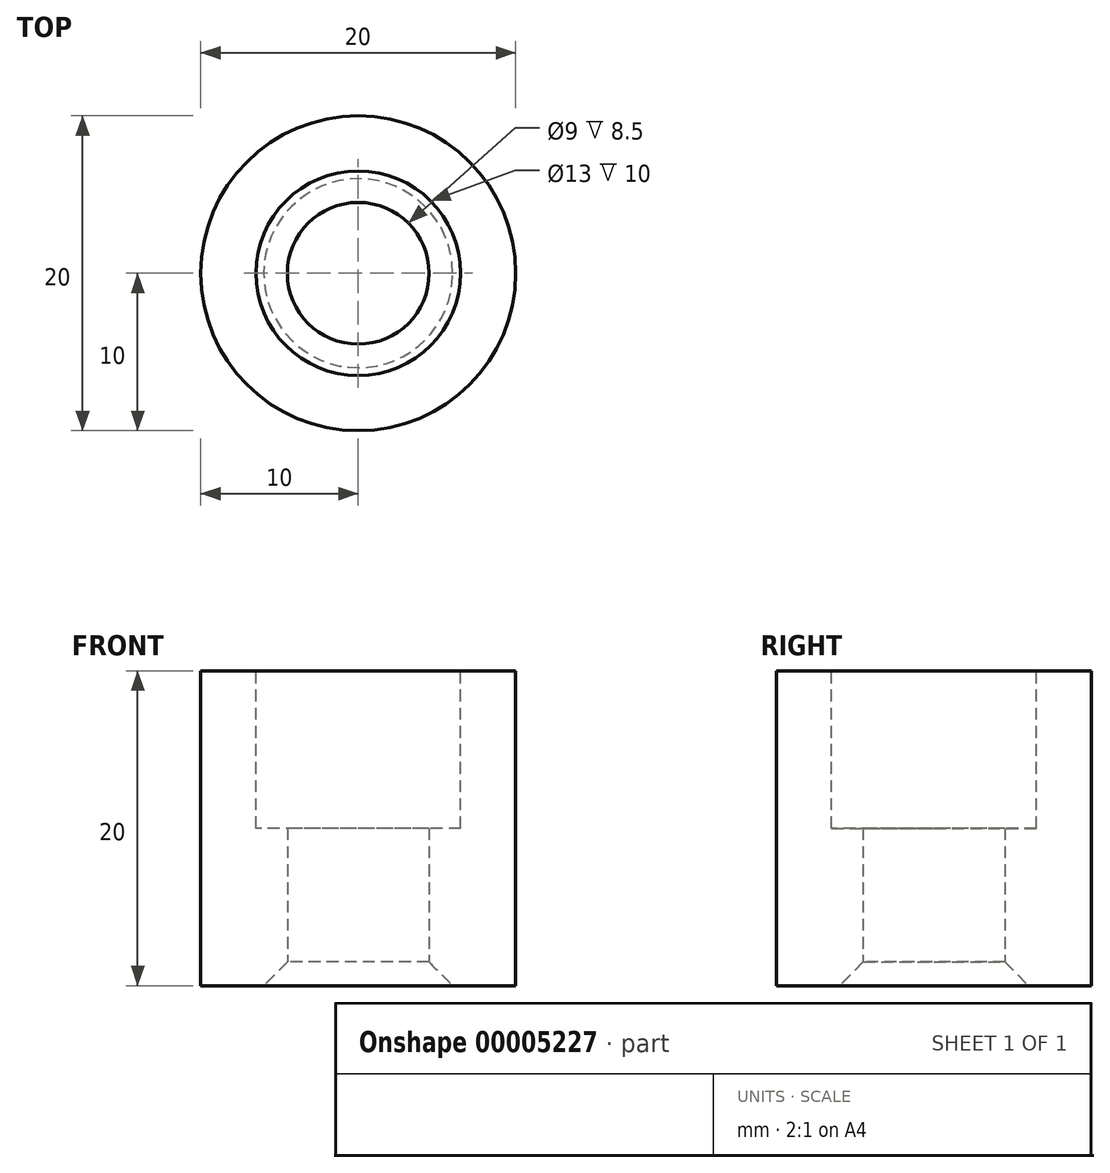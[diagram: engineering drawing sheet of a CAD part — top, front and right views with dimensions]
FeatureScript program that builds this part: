
annotation { "Feature Type Name" : "Feature", "Feature Type Description" : "" }
export const myFeature = defineFeature(function(context is Context, id is Id, definition is map)
    precondition{}
    {
        {
            var Q0;
            Q0=qCreatedBy(makeId("Top.planeOp"),FACE);
            var sketch = newSketch(context, id + "F0", { "sketchPlane" : qUnion([Q0])});
            skCircle(sketch, "E0", {"center": v(0, 0) * mm, "radius": 10 * mm});
            skCircle(sketch, "E1", {"center": v(0, 0) * mm, "radius": 4.5 * mm});
            skSolve(sketch);
        }
        {
            var Q0;
            Q0=makeQuery(id+"F0.imprint","IMPRINT",FACE,{"disambiguationData":[TD([[makeQuery(id+"F0.imprint","IMPRINT",EDGE,{"derivedFrom":sQuery(id+"F0.wireOp",EDGE,"E0")}),1.0]])]});
            extrude(context, id + "F1", {"entities" : qUnion([Q0]), "depth" : 10 * mm});
        }
        {
            var Q0;
            Q0=makeQuery(id+"F1.opExtrude","CAP_FACE",FACE,{"disambiguationData":[OSD([sQuery(id+"F0.wireOp",EDGE,"E0"),sQuery(id+"F0.wireOp",EDGE,"E1")])],"isStart":false});
            var sketch = newSketch(context, id + "F2", { "sketchPlane" : qUnion([Q0])});
            skCircle(sketch, "E2", {"center": v(0, 0) * mm, "radius": 6.5 * mm});
            skCircle(sketch, "E3", {"center": v(0, 0) * mm, "radius": 10 * mm});
            skSolve(sketch);
        }
        {
            var Q0;
            {var subQ0=makeQuery(id+"F2.imprint","IMPRINT",EDGE,{"derivedFrom":sQuery(id+"F2.wireOp",EDGE,"E2")});var subQ1=makeQuery(id+"F2.imprint","IMPRINT",EDGE,{"derivedFrom":makeQuery(id+"F1.opExtrude","CAP_EDGE",EDGE,{"disambiguationData":[OSD([sQuery(id+"F0.wireOp",EDGE,"E1")])],"isStart":false})});Q0=qUnion([makeQuery(id+"F2.imprint","IMPRINT",FACE,{"disambiguationData":[TD([[subQ0,-1.0]])]}),makeQuery(id+"F2.imprint","IMPRINT",FACE,{"disambiguationData":[TD([[subQ1,1.0]])]}),makeQuery(id+"F2.imprint","IMPRINT",FACE,{"disambiguationData":[TD([[subQ0,1.0]])]})]);}
            extrude(context, id + "F3", {"entities" : qUnion([Q0]), "operationType" : NewBodyOperationType.ADD, "depth" : 10 * mm});
        }
        {
            var Q0;
            Q0=makeQuery(id+"F3.opExtrude","CAP_FACE",FACE,{"disambiguationData":[OSD([sQuery(id+"F2.wireOp",EDGE,"E3")])],"isStart":false});
            var sketch = newSketch(context, id + "F4", { "sketchPlane" : qUnion([Q0])});
            skCircle(sketch, "E4", {"center": v(0, 0) * mm, "radius": 6.5 * mm});
            skSolve(sketch);
        }
        {
            var Q0;
            Q0=makeQuery(id+"F4.imprint","IMPRINT",FACE,{"disambiguationData":[TD([[makeQuery(id+"F4.imprint","IMPRINT",EDGE,{"derivedFrom":sQuery(id+"F4.wireOp",EDGE,"E4")}),1.0]])]});
            var Q1;
            Q1=makeQuery(id+"F3.opExtrude","CAP_FACE",FACE,{"disambiguationData":[OSD([sQuery(id+"F2.wireOp",EDGE,"E3")])],"isStart":true});
            extrude(context, id + "F5", {"entities" : qUnion([Q0]), "operationType" : NewBodyOperationType.REMOVE, "endBound" : BoundingType.UP_TO_SURFACE, "oppositeDirection" : true, "endBoundEntityFace" : qUnion([Q1]), "depth" : 25 * mm});
        }
        {
            var Q0;
            Q0=makeQuery(id+"F1.opExtrude","CAP_EDGE",EDGE,{"disambiguationData":[OSD([sQuery(id+"F0.wireOp",EDGE,"E1")])],"isStart":true});
            var Q1;
            Q1=makeQuery(id+"F5.boolean.opBoolean","COPY",EDGE,{"derivedFrom":makeQuery(id+"F5.opExtrude","CAP_EDGE",EDGE,{"disambiguationData":[OSD([sQuery(id+"F4.wireOp",EDGE,"E4")])],"isStart":true})});
            chamfer(context, id + "F6", {"entities" : qUnion([Q0, Q1]), "width" : 1.5 * mm, "tangentPropagation" : true});
        }
    });
